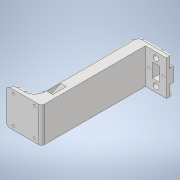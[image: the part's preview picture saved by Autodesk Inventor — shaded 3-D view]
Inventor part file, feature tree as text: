
AUTODESK INVENTOR PART (.ipt)
format: ipt  version: 2022.3 (Build 263350000, 350)  size: 402,432 bytes
history: native  units: mm
features: sketch x13, extrude x7, fillet x4, hole x2, sweep x2, emboss x1
ambient origin geometry x8: Origin, YZ Plane, XZ Plane, XY Plane, X Axis, Y Axis, Z Axis, Center Point
bodies: Solid1 (feature_tree)
feature tree (29):
  extrude  "Extrusion1"  Depth=10.0mm
  fillet  "Fillet1"  Radius=50.0mm
  fillet  "Fillet2"  Radius=10.0mm
  fillet  "Fillet3"  Radius=50.0mm
  extrude  "Extrusion2"  Depth=10.0mm TaperAngle=0.0deg
  hole  "Hole1"  [1 undecoded]
  sweep  "Sweep1"
  sweep  "Sweep2"
  sketch  "Sketch8"  dims[d18=5.0mm d19=3.4mm d20=3.4mm]
  extrude  "Extrusion3"  Depth=40.0mm
  extrude  "Extrusion4"  Depth=40.0mm
  extrude  "Extrusion5"  Depth=3.4mm
  fillet  "Fillet5"  Radius=3.4mm
  emboss  "Emboss1"
  hole  "Hole4"  [1 undecoded]
  extrude  "Extrusion6"  Depth=6.0mm
  extrude  "Extrusion7"  Depth=20.0mm
  sketch  "Sketch1"  dims[d0=20.0mm d1=148.0mm d2=50.0mm d3=10.0mm d4=50.0mm]
  sketch  "Sketch2"  dims[d5=10.0mm d6=50.0mm d7=0.0mm]
  sketch  "Sketch3"  dims[d8=10.0mm d9=5.0mm]
  sketch  "Sketch4"  dims[d10=10.0mm d11=10.0mm]
  sketch  "Sketch5"  dims[d12=5.0mm d13=10.0mm]
  sketch  "Sketch6"  dims[d14=5.0mm d15=40.0mm]
  sketch  "Sketch7"  dims[d16=5.0mm d17=40.0mm]
  sketch  "Sketch9"  dims[d21=3.4mm d22=3.4mm]
  sketch  "Sketch12"  dims[d23=50.0mm d24=0.0mm]
  sketch  "Sketch13"  dims[d25=3.4mm d26=6.0mm d27=6.0mm d28=2.0mm d29=90.0deg d30=2.2mm d31=0.0mm d32=8.0mm]
  sketch  "Sketch14"  dims[d33=8.0mm d34=20.0mm]
  sketch  "Sketch15"  dims[d35=5.0mm d36=20.0mm d37=9.0mm d38=0.0mm d39=0.0mm d40=0.0mm d41=0.0mm d42=8.0mm d43=8.0mm d44=20.0mm d45=5.0mm d46=20.0mm d47=9.0mm d48=0.0mm d49=0.0mm d50=10.0mm d51=20.0mm d52=8.0mm d53=8.0mm d54=5.0mm d55=0.0mm d56=0.0mm d57=0.0mm d58=12.0mm d59=12.0mm d60=2.0mm d61=0.0mm d77=4.0mm d78=128.0mm d79=40.0mm d80=0.0mm d81=0.0mm d82=1.0mm d83=0.0mm d85=5.0mm d86=5.0mm d87=3.4mm d88=6.0mm d89=4.1mm d90=5.1mm d91=90.0deg d92=0.9mm d93=0.0mm d94=6.0mm d95=6.0mm d96=15.0mm d97=0.0mm d98=6.0mm d99=6.0mm d100=15.0mm d101=0.0mm d76=0.0mm]
note: 2 required parameter values undecoded (feature->parameter linkage not recoverable at this tier; creation-order binding heuristic only, values carry confidence <= 0.55)
